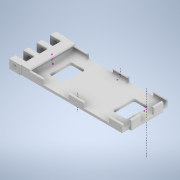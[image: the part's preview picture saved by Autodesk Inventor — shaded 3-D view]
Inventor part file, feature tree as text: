
AUTODESK INVENTOR PART (.ipt)
format: ipt  version: 2020 (Build 240168000, 168)  size: 727,552 bytes
history: native  units: mm
features: projected_geometry x18, sketch x14, extrude x12, other x3
ambient origin geometry x8: Origin, YZ Plane, XZ Plane, XY Plane, X Axis, Y Axis, Z Axis, Center Point
bodies: Solid1 (feature_tree)
feature tree (47):
  other  "Part9.1.ipt"
  extrude  "Extrusion1"  Depth=0.405517mm TaperAngle=0.0deg
  extrude  "Extrusion2"  Depth=15.5mm TaperAngle=0.0deg
  extrude  "Extrusion3"  Depth=20.0mm TaperAngle=0.0deg
  extrude  "Extrusion4"  Depth=40.0mm
  extrude  "Extrusion5"  Depth=12.0mm
  sketch  "Sketch10"  dims[d70=5.0mm d71=8.75mm]
  extrude  "Extrusion8"  Depth=8.75mm
  sketch  "Sketch22"  dims[d72=1.0mm d73=0.0mm d74=1.0mm d75=0.0mm]
  sketch  "Sketch23"  dims[d76=597.5mm d77=0.0mm d88=97.5mm d89=0.0mm]
  extrude  "Extrusion15"  Depth=1.0mm TaperAngle=0.0deg
  sketch  "Sketch27"  dims[d92=8.3mm d93=8.3mm]
  extrude  "Extrusion16"  Depth=97.5mm TaperAngle=0.0deg
  extrude  "Extrusion17"  Depth=17.25mm
  extrude  "Extrusion18"  Depth=8.3mm
  extrude  "Extrusion19"  Depth=12.8mm
  extrude  "Extrusion20"  Depth=9.591003mm
  other  "Solid2::Part9.1.ipt"
  other  "TaggingFeature1"
  sketch  "Sketch1"  dims[d0=0.405517mm d1=50.68mm d2=0.0mm]
  sketch  "Sketch3"  dims[d7=8.5mm d8=0.0mm d9=15.5mm d10=0.0mm]
  projected_geometry  "Projected Loop1"
  sketch  "Sketch5"  dims[d15=15.5mm d16=0.0mm d17=20.0mm d18=0.0mm]
  sketch  "Sketch6"  dims[d36=141.75mm d37=0.0mm d60=40.0mm]
  sketch  "Sketch7"  dims[d61=40.0mm d63=12.0mm]
  projected_geometry  "Projected Loop3"
  projected_geometry  "Projected Loop16"
  projected_geometry  "Projected Loop17"
  projected_geometry  "Projected Loop18"
  projected_geometry  "Projected Loop19"
  projected_geometry  "Projected Loop20"
  projected_geometry  "Projected Loop22"
  sketch  "Sketch26"  dims[d90=6.4mm d91=17.25mm]
  projected_geometry  "Projected Loop26"
  projected_geometry  "Projected Loop27"
  sketch  "Sketch28"  dims[d94=12.8mm d95=12.8mm]
  projected_geometry  "Projected Loop28"
  sketch  "Sketch29"  dims[d96=9.591003mm d98=9.591003mm]
  projected_geometry  "Projected Loop29"
  sketch  "Sketch30"  dims[d99=20.0mm]
  projected_geometry  "Projected Loop30"
  projected_geometry  "Projected Loop31"
  projected_geometry  "Projected Loop32"
  sketch  "Sketch31"  dims[d100=97.5mm d101=0.0mm d108=2.783mm d109=0.0mm d56=0.5mm d57=0.872665mm d58=0.5mm d59=0.872665mm d102=0.5mm d103=0.872665mm d104=0.5mm d105=0.872665mm]
  projected_geometry  "Projected Loop33"
  projected_geometry  "Projected Loop34"
  projected_geometry  "Projected Loop35"
